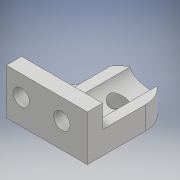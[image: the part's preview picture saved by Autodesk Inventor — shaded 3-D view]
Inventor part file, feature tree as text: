
AUTODESK INVENTOR PART (.ipt)
format: ipt  version: 2018.2 (Build 222227000, 227)  size: 166,912 bytes
history: native  units: mm
features: sketch x5, extrude x5
ambient origin geometry x8: Origin, YZ Plane, XZ Plane, XY Plane, X Axis, Y Axis, Z Axis, Center Point
bodies: Solid1 (feature_tree)
feature tree (10):
  sketch  "Sketch1"  dims[d9=4.5mm d10=0.0mm d11=4.5mm d12=0.0mm]
  extrude  "Extrusion1"  Depth=4.5mm TaperAngle=0.0deg
  extrude  "Extrusion2"  Depth=3.2mm
  extrude  "Extrusion3"  Depth=3.0mm
  extrude  "Extrusion4"  TaperAngle=90.0deg  [1 undecoded]
  extrude  "Extrusion5"  Depth=10.0mm
  sketch  "Sketch4"  dims[d13=3.2mm d14=3.2mm]
  sketch  "Sketch5"  dims[d15=5.5mm d16=0.0mm d17=3.0mm]
  sketch  "Sketch6"  dims[d19=11.5mm d23=90.0deg]
  sketch  "Sketch7"  dims[d25=12.5mm d31=5.5mm d32=150.0deg d34=6.0mm d35=6.0mm d36=10.0mm d37=0.0mm d38=5.0mm d39=5.0mm d40=5.0mm d41=5.0mm d42=10.0mm d43=0.0mm d46=2.75mm d47=0.0mm d49=3.2mm d50=8.0mm]
note: 1 required parameter value undecoded (feature->parameter linkage not recoverable at this tier; creation-order binding heuristic only, values carry confidence <= 0.55)
